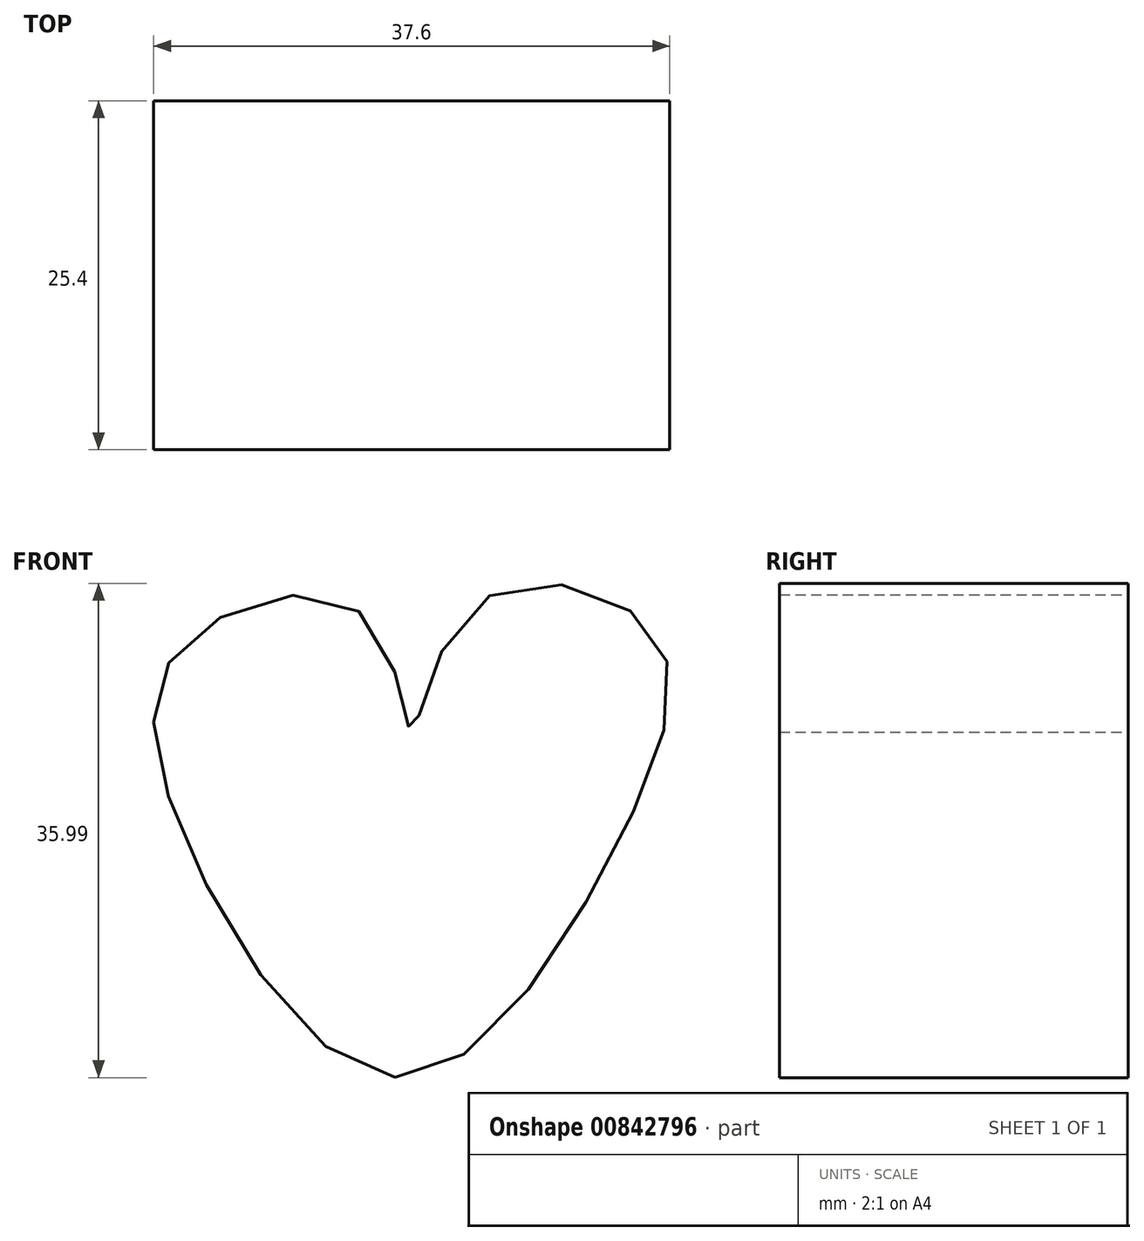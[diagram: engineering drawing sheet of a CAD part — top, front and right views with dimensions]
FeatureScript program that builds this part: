
annotation { "Feature Type Name" : "Feature", "Feature Type Description" : "" }
export const myFeature = defineFeature(function(context is Context, id is Id, definition is map)
    precondition{}
    {
        {
            var Q0;
            Q0=qCreatedBy(makeId("Front.planeOp"),FACE);
            var sketch = newSketch(context, id + "F0", { "sketchPlane" : qUnion([Q0])});
            skFitSpline(sketch, "E0", {"points": [v(-43.31, 17.2) * mm, v(-59.11, 35.74) * mm, v(-58.71, 48.74) * mm, v(-45.64, 50.87) * mm, v(-42.12, 42.36) * mm, v(-37.65, 51.47) * mm, v(-24.69, 49.82) * mm, v(-27.27, 33.94) * mm, v(-43.31, 17.2) * mm]});
            skSolve(sketch);
        }
        {
            var Q0;
            Q0=makeQuery(id+"F0.imprint","IMPRINT",FACE,{"disambiguationData":[TD([[makeQuery(id+"F0.imprint","IMPRINT",EDGE,{"derivedFrom":sQuery(id+"F0.wireOp",EDGE,"E0")}),-1.0]])]});
            extrude(context, id + "F1", {"entities" : qUnion([Q0]), "depth" : 25.4 * mm, "offsetDistance" : 25.4 * mm});
        }
    });
